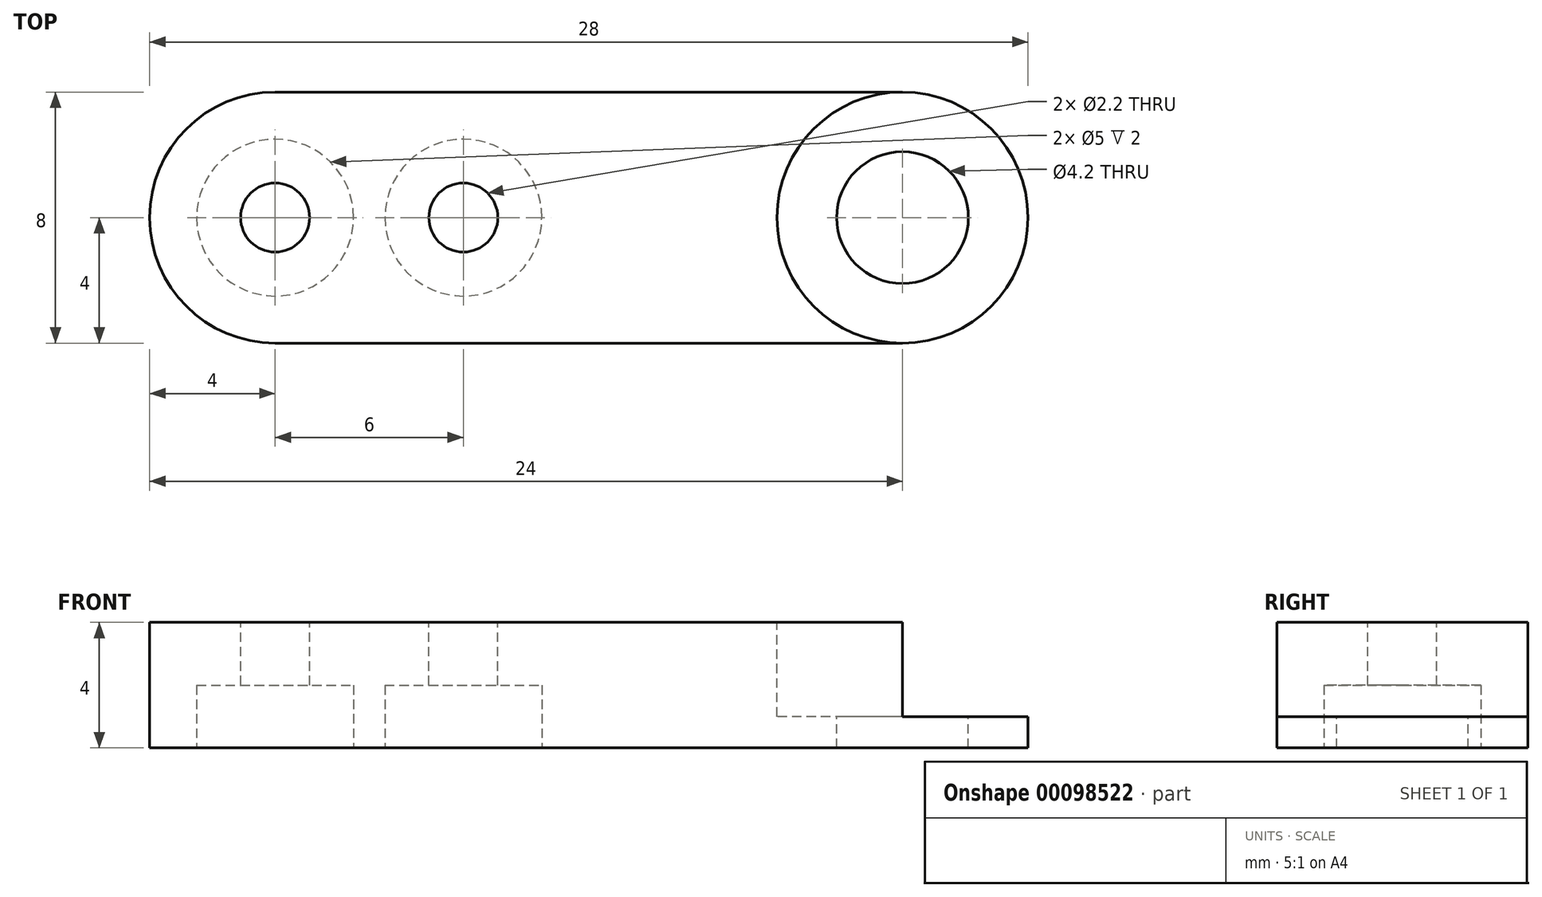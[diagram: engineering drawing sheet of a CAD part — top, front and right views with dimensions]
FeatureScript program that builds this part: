
annotation { "Feature Type Name" : "Feature", "Feature Type Description" : "" }
export const myFeature = defineFeature(function(context is Context, id is Id, definition is map)
    precondition{}
    {
        {
            var Q0;
            Q0=qCreatedBy(makeId("Top.planeOp"),FACE);
            var sketch = newSketch(context, id + "F0", { "sketchPlane" : qUnion([Q0])});
            skLineSegment(sketch, "E0", {"start": v(0, 0) * mm, "end": v(6, 0) * mm});
            skCircle(sketch, "E1", {"center": v(0, 0) * mm, "radius": 1.1 * mm});
            skCircle(sketch, "E2", {"center": v(6, 0) * mm, "radius": 1.1 * mm});
            skLineSegment(sketch, "E3", {"start": v(6, 0) * mm, "end": v(20, 0) * mm});
            skCircle(sketch, "E4", {"center": v(20, 0) * mm, "radius": 2.1 * mm});
            skCircle(sketch, "E5", {"center": v(20, 0) * mm, "radius": 4 * mm});
            skCircle(sketch, "E6", {"center": v(0, 0) * mm, "radius": 4 * mm});
            skLineSegment(sketch, "E7", {"start": v(0, 0) * mm, "end": v(0, 4) * mm});
            skLineSegment(sketch, "E8", {"start": v(0, 4) * mm, "end": v(20, 4) * mm});
            skLineSegment(sketch, "E9", {"start": v(20, 4) * mm, "end": v(20, -4) * mm});
            skLineSegment(sketch, "E10", {"start": v(20, -4) * mm, "end": v(0, -4) * mm});
            skSolve(sketch);
        }
        {
            var Q0;
            Q0 = qSketchRegion(id + "F0", true);
            extrude(context, id + "F1", {"entities" : qUnion([Q0]), "oppositeDirection" : true, "depth" : 4 * mm});
        }
        {
            var Q0;
            {var subQ0=sQuery(id+"F0.wireOp",EDGE,"E5");var subQ1=sQuery(id+"F0.wireOp",EDGE,"E3");var subQ2=makeQuery(id+"F0.imprint","INTERSECT",VERTEX,{"derivedFrom":[subQ1,subQ0]});Q0=makeQuery(id+"F0.imprint","IMPRINT",FACE,{"disambiguationData":[TD([[makeQuery(id+"F0.imprint","IMPRINT",EDGE,{"disambiguationData":[TD([[subQ2,-1.0]])],"derivedFrom":subQ1}),-1.0]])]});}
            var Q1;
            {var subQ0=sQuery(id+"F0.wireOp",EDGE,"E5");var subQ1=sQuery(id+"F0.wireOp",EDGE,"E3");var subQ2=makeQuery(id+"F0.imprint","INTERSECT",VERTEX,{"derivedFrom":[subQ1,subQ0]});Q1=makeQuery(id+"F0.imprint","IMPRINT",FACE,{"disambiguationData":[TD([[makeQuery(id+"F0.imprint","IMPRINT",EDGE,{"disambiguationData":[TD([[subQ2,-1.0]])],"derivedFrom":subQ1}),1.0]])]});}
            var Q2;
            {var subQ0=sQuery(id+"F0.wireOp",EDGE,"E9");var subQ1=sQuery(id+"F0.wireOp",EDGE,"E4");var subQ2=makeQuery(id+"F0.imprint","INTERSECT",VERTEX,{"disambiguationData":[OD(0.0)],"derivedFrom":[subQ1,subQ0]});Q2=makeQuery(id+"F0.imprint","IMPRINT",FACE,{"disambiguationData":[TD([[makeQuery(id+"F0.imprint","IMPRINT",EDGE,{"disambiguationData":[TD([[subQ2,1.0]])],"derivedFrom":subQ1}),-1.0]])]});}
            extrude(context, id + "F2", {"entities" : qUnion([Q0, Q1, Q2]), "operationType" : NewBodyOperationType.REMOVE, "oppositeDirection" : true, "depth" : 3 * mm});
        }
        {
            var Q0;
            Q0=makeQuery(id+"F1.opExtrude","CAP_FACE",FACE,{"disambiguationData":[OSD([sQuery(id+"F0.wireOp",EDGE,"E1"),sQuery(id+"F0.wireOp",EDGE,"E2"),sQuery(id+"F0.wireOp",EDGE,"E4"),sQuery(id+"F0.wireOp",EDGE,"E5"),sQuery(id+"F0.wireOp",EDGE,"E6"),sQuery(id+"F0.wireOp",EDGE,"E8"),sQuery(id+"F0.wireOp",EDGE,"E10")])],"isStart":false});
            var sketch = newSketch(context, id + "F3", { "sketchPlane" : qUnion([Q0])});
            skCircle(sketch, "E11", {"center": v(6, 0) * mm, "radius": 2.5 * mm});
            skCircle(sketch, "E12", {"center": v(0, 0) * mm, "radius": 2.5 * mm});
            skSolve(sketch);
        }
        {
            var Q0;
            Q0 = qSketchRegion(id + "F3", true);
            extrude(context, id + "F4", {"entities" : qUnion([Q0]), "operationType" : NewBodyOperationType.REMOVE, "oppositeDirection" : true, "depth" : 2 * mm});
        }
    });
